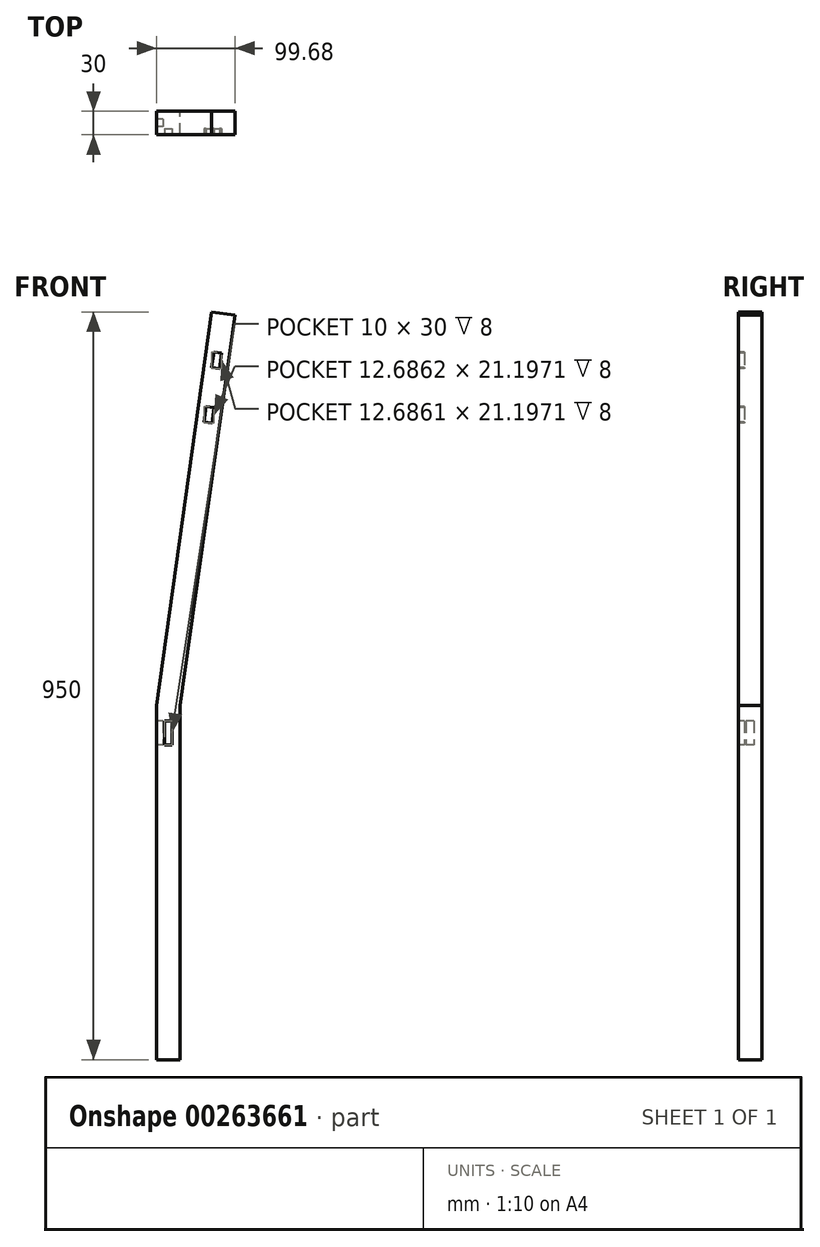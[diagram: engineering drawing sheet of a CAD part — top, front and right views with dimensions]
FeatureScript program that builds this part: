
annotation { "Feature Type Name" : "Feature", "Feature Type Description" : "" }
export const myFeature = defineFeature(function(context is Context, id is Id, definition is map)
    precondition{}
    {
        {
            var Q0;
            Q0=qCreatedBy(makeId("Front.planeOp"),FACE);
            var sketch = newSketch(context, id + "F0", { "sketchPlane" : qUnion([Q0])});
            skLineSegment(sketch, "E0", {"start": v(0, 0) * mm, "end": v(0, -450) * mm});
            skLineSegment(sketch, "E1", {"start": v(0, -450) * mm, "end": v(30, -450) * mm});
            skLineSegment(sketch, "E2", {"start": v(30, -450) * mm, "end": v(30, 0) * mm});
            skLineSegment(sketch, "E3", {"start": v(30, 0) * mm, "end": v(99.68, 495.82) * mm});
            skLineSegment(sketch, "E4", {"start": v(99.68, 495.82) * mm, "end": v(69.98, 500) * mm});
            skLineSegment(sketch, "E5", {"start": v(69.98, 500) * mm, "end": v(0, 0) * mm});
            skSolve(sketch);
        }
        {
            var Q0;
            Q0=qSketchRegion(id+"F0",true);
            extrude(context, id + "F1", {"entities" : qUnion([Q0]), "depth" : 30 * mm});
        }
        {
            var Q0;
            Q0=makeQuery(id+"F1.opExtrude","CAP_FACE",FACE,{"disambiguationData":[OSD([sQuery(id+"F0.wireOp",EDGE,"E0"),sQuery(id+"F0.wireOp",EDGE,"E1"),sQuery(id+"F0.wireOp",EDGE,"E2"),sQuery(id+"F0.wireOp",EDGE,"E3"),sQuery(id+"F0.wireOp",EDGE,"E4"),sQuery(id+"F0.wireOp",EDGE,"E5")])],"isStart":false});
            var sketch = newSketch(context, id + "F2", { "sketchPlane" : qUnion([Q0])});
            skLineSegment(sketch, "E6.bottom", {"start": v(10, -20) * mm, "end": v(20, -20) * mm});
            skLineSegment(sketch, "E6.top", {"start": v(10, -50) * mm, "end": v(20, -50) * mm});
            skLineSegment(sketch, "E6.left", {"start": v(10, -20) * mm, "end": v(10, -50) * mm});
            skLineSegment(sketch, "E6.right", {"start": v(20, -20) * mm, "end": v(20, -50) * mm});
            skSolve(sketch);
        }
        {
            var Q0;
            Q0=qSketchRegion(id+"F2",true);
            extrude(context, id + "F3", {"entities" : qUnion([Q0]), "operationType" : NewBodyOperationType.REMOVE, "oppositeDirection" : true, "depth" : 8 * mm});
        }
        {
            var Q0;
            Q0=makeQuery(id+"F1.opExtrude","CAP_FACE",FACE,{"disambiguationData":[OSD([sQuery(id+"F0.wireOp",EDGE,"E0"),sQuery(id+"F0.wireOp",EDGE,"E1"),sQuery(id+"F0.wireOp",EDGE,"E2"),sQuery(id+"F0.wireOp",EDGE,"E3"),sQuery(id+"F0.wireOp",EDGE,"E4"),sQuery(id+"F0.wireOp",EDGE,"E5")])],"isStart":false});
            var sketch = newSketch(context, id + "F4", { "sketchPlane" : qUnion([Q0])});
            skLineSegment(sketch, "E7.bottom", {"start": v(72.92, 449.1) * mm, "end": v(82.82, 447.7) * mm});
            skLineSegment(sketch, "E7.top", {"start": v(70.14, 429.29) * mm, "end": v(80.04, 427.9) * mm});
            skLineSegment(sketch, "E7.left", {"start": v(72.92, 449.1) * mm, "end": v(70.14, 429.29) * mm});
            skLineSegment(sketch, "E7.right", {"start": v(82.82, 447.7) * mm, "end": v(80.04, 427.9) * mm});
            skLineSegment(sketch, "E8.bottom", {"start": v(63.18, 379.78) * mm, "end": v(73.08, 378.38) * mm});
            skLineSegment(sketch, "E8.top", {"start": v(60.4, 359.97) * mm, "end": v(70.3, 358.58) * mm});
            skLineSegment(sketch, "E8.left", {"start": v(63.18, 379.78) * mm, "end": v(60.4, 359.97) * mm});
            skLineSegment(sketch, "E8.right", {"start": v(73.08, 378.38) * mm, "end": v(70.3, 358.58) * mm});
            skSolve(sketch);
        }
        {
            var Q0;
            Q0=qSketchRegion(id+"F4",true);
            extrude(context, id + "F5", {"entities" : qUnion([Q0]), "operationType" : NewBodyOperationType.REMOVE, "oppositeDirection" : true, "depth" : 8 * mm});
        }
        {
            var Q0;
            Q0=makeQuery(id+"F1.opExtrude","SWEPT_FACE",FACE,{"disambiguationData":[OSD([sQuery(id+"F0.wireOp",EDGE,"E0")])]});
            var sketch = newSketch(context, id + "F6", { "sketchPlane" : qUnion([Q0])});
            skLineSegment(sketch, "E9.bottom", {"start": v(10, -20) * mm, "end": v(20, -20) * mm});
            skLineSegment(sketch, "E9.top", {"start": v(10, -50) * mm, "end": v(20, -50) * mm});
            skLineSegment(sketch, "E9.left", {"start": v(10, -20) * mm, "end": v(10, -50) * mm});
            skLineSegment(sketch, "E9.right", {"start": v(20, -20) * mm, "end": v(20, -50) * mm});
            skSolve(sketch);
        }
        {
            var Q0;
            Q0=qSketchRegion(id+"F6",true);
            extrude(context, id + "F7", {"entities" : qUnion([Q0]), "operationType" : NewBodyOperationType.REMOVE, "oppositeDirection" : true, "depth" : 8 * mm});
        }
    });
